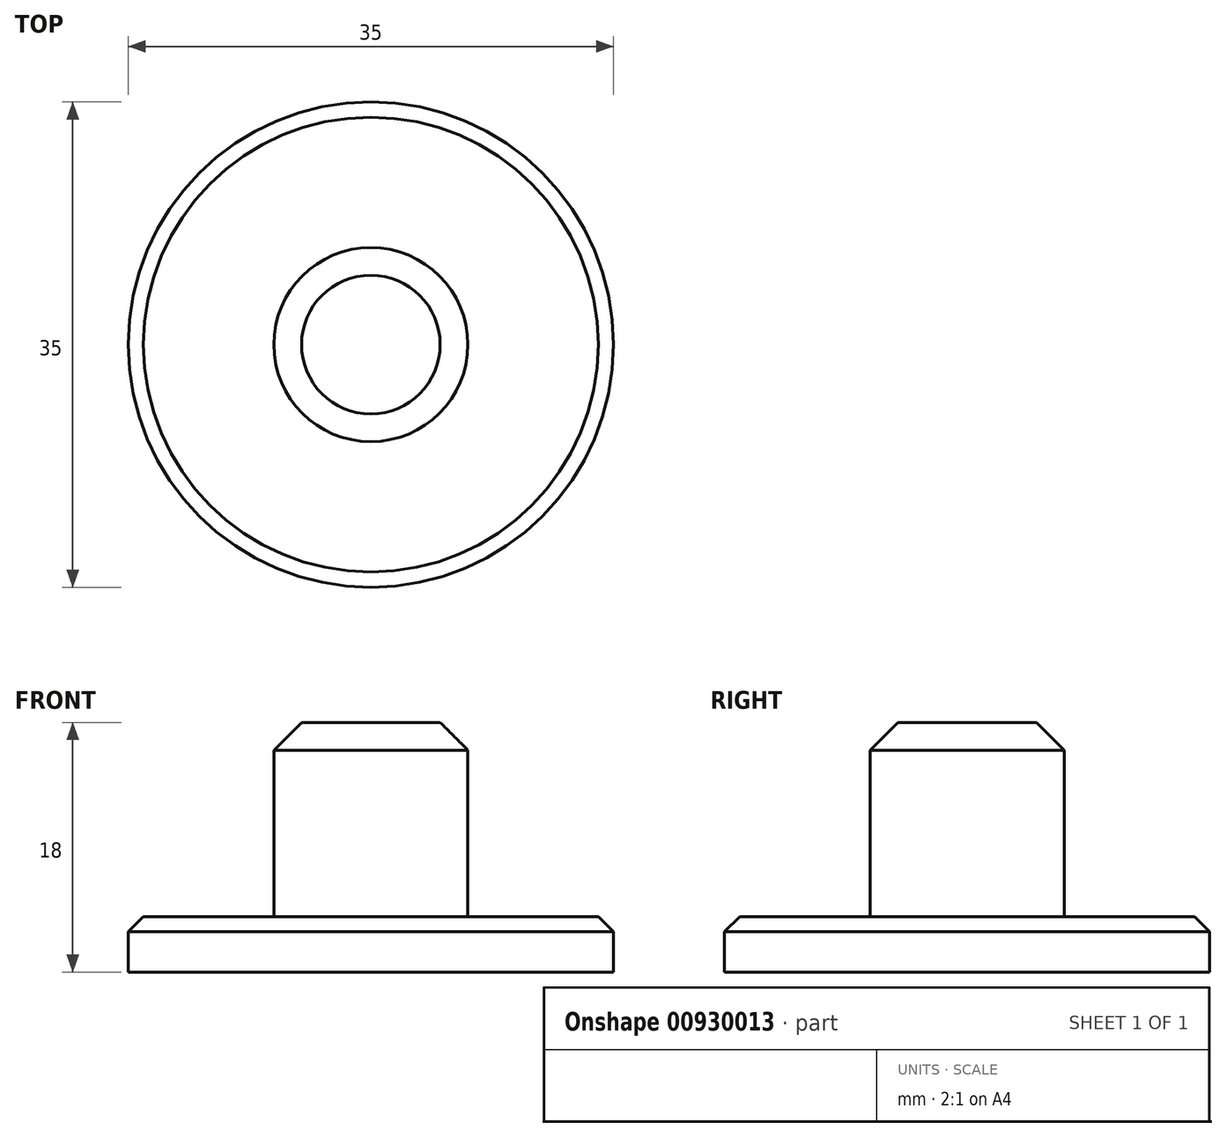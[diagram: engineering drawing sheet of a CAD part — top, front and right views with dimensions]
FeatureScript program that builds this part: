
annotation { "Feature Type Name" : "Feature", "Feature Type Description" : "" }
export const myFeature = defineFeature(function(context is Context, id is Id, definition is map)
    precondition{}
    {
        {
            var Q0;
            Q0=qCreatedBy(makeId("Top.planeOp"),FACE);
            var sketch = newSketch(context, id + "F0", { "sketchPlane" : qUnion([Q0])});
            skCircle(sketch, "E0", {"center": v(0, 0) * mm, "radius": 17.5 * mm});
            skSolve(sketch);
        }
        {
            var Q0;
            Q0 = qSketchRegion(id + "F0", true);
            extrude(context, id + "F1", {"entities" : qUnion([Q0]), "depth" : 4 * mm, "offsetDistance" : 25 * mm});
        }
        {
            var Q0;
            Q0=makeQuery(id+"F1.opExtrude","CAP_FACE",FACE,{"disambiguationData":[OSD([sQuery(id+"F0.wireOp",EDGE,"E0")])],"isStart":false});
            var sketch = newSketch(context, id + "F2", { "sketchPlane" : qUnion([Q0])});
            skCircle(sketch, "E1", {"center": v(0, 0) * mm, "radius": 7 * mm});
            skSolve(sketch);
        }
        {
            var Q0;
            Q0 = qSketchRegion(id + "F2", true);
            extrude(context, id + "F3", {"entities" : qUnion([Q0]), "operationType" : NewBodyOperationType.ADD, "depth" : 14 * mm, "offsetDistance" : 25 * mm});
        }
        {
            var Q0;
            Q0=makeQuery(id+"F1.opExtrude","CAP_EDGE",EDGE,{"disambiguationData":[OSD([sQuery(id+"F0.wireOp",EDGE,"E0")])],"isStart":false});
            chamfer(context, id + "F4", {"entities" : qUnion([Q0]), "width" : 1.1 * mm, "tangentPropagation" : true});
        }
        {
            var Q0;
            Q0=makeQuery(id+"F3.opExtrude","CAP_FACE",FACE,{"disambiguationData":[OSD([sQuery(id+"F2.wireOp",EDGE,"E1")])],"isStart":false});
            var Q1;
            Q1=makeQuery(id+"F3.opExtrude","CAP_EDGE",EDGE,{"disambiguationData":[OSD([sQuery(id+"F2.wireOp",EDGE,"E1")])],"isStart":true});
            chamfer(context, id + "F5", {"entities" : qUnion([Q0, Q1]), "width" : 2 * mm, "tangentPropagation" : true});
        }
    });
